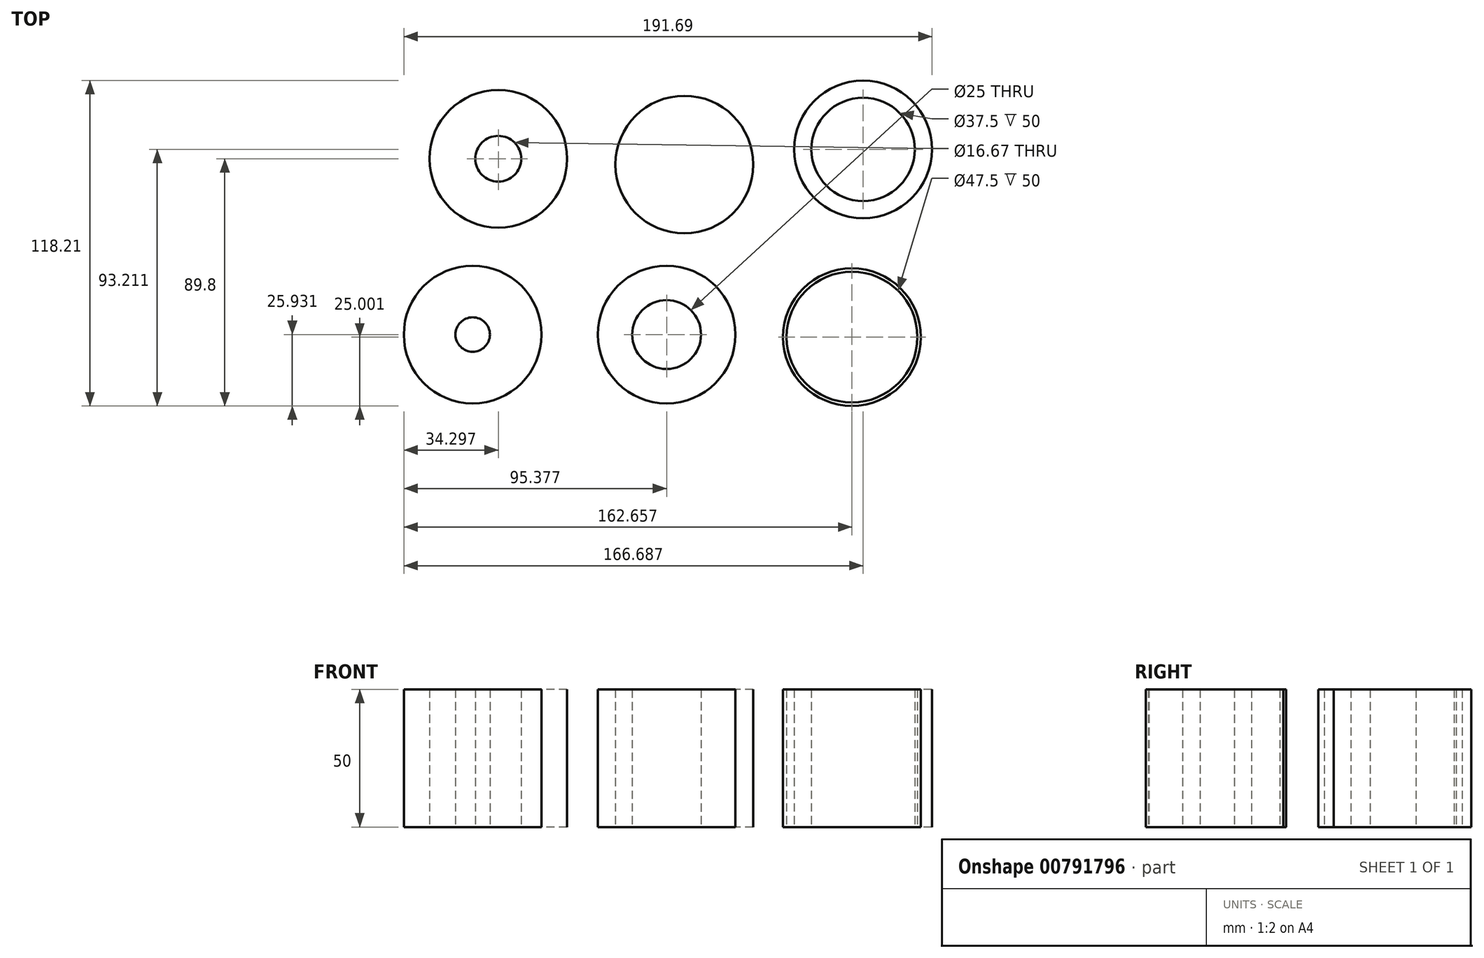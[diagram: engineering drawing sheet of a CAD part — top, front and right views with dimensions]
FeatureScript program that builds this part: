
annotation { "Feature Type Name" : "Feature", "Feature Type Description" : "" }
export const myFeature = defineFeature(function(context is Context, id is Id, definition is map)
    precondition{}
    {
        {
            var Q0;
            Q0=qCreatedBy(makeId("Top.planeOp"),FACE);
            var sketch = newSketch(context, id + "F0", { "sketchPlane" : qUnion([Q0])});
            skCircle(sketch, "E0", {"center": v(-30.83, 32.84) * mm, "radius": 25 * mm});
            skCircle(sketch, "E1", {"center": v(34.04, 38.36) * mm, "radius": 25 * mm});
            skCircle(sketch, "E2", {"center": v(30, -29.85) * mm, "radius": 25 * mm});
            skCircle(sketch, "E3", {"center": v(-37.27, -28.92) * mm, "radius": 25 * mm});
            skCircle(sketch, "E4", {"center": v(-98.35, 34.95) * mm, "radius": 25 * mm});
            skCircle(sketch, "E5", {"center": v(-107.65, -28.92) * mm, "radius": 25 * mm});
            skCircle(sketch, "E6", {"center": v(30, -29.85) * mm, "radius": 23.75 * mm});
            skCircle(sketch, "E7", {"center": v(34.04, 38.36) * mm, "radius": 18.75 * mm});
            skCircle(sketch, "E8", {"center": v(-37.27, -28.92) * mm, "radius": 12.5 * mm});
            skCircle(sketch, "E9", {"center": v(-107.65, -28.92) * mm, "radius": 6.25 * mm});
            skCircle(sketch, "E10", {"center": v(-98.35, 34.95) * mm, "radius": 8.33 * mm});
            skSolve(sketch);
        }
        {
            var Q0;
            Q0=makeQuery(id+"F0.imprint","IMPRINT",FACE,{"disambiguationData":[TD([[makeQuery(id+"F0.imprint","IMPRINT",EDGE,{"derivedFrom":sQuery(id+"F0.wireOp",EDGE,"E4")}),1.0]])]});
            var Q1;
            Q1=makeQuery(id+"F0.imprint","IMPRINT",FACE,{"disambiguationData":[TD([[makeQuery(id+"F0.imprint","IMPRINT",EDGE,{"derivedFrom":sQuery(id+"F0.wireOp",EDGE,"E0")}),1.0]])]});
            var Q2;
            Q2=makeQuery(id+"F0.imprint","IMPRINT",FACE,{"disambiguationData":[TD([[makeQuery(id+"F0.imprint","IMPRINT",EDGE,{"derivedFrom":sQuery(id+"F0.wireOp",EDGE,"E1")}),1.0]])]});
            var Q3;
            Q3=makeQuery(id+"F0.imprint","IMPRINT",FACE,{"disambiguationData":[TD([[makeQuery(id+"F0.imprint","IMPRINT",EDGE,{"derivedFrom":sQuery(id+"F0.wireOp",EDGE,"E5")}),1.0]])]});
            var Q4;
            Q4=makeQuery(id+"F0.imprint","IMPRINT",FACE,{"disambiguationData":[TD([[makeQuery(id+"F0.imprint","IMPRINT",EDGE,{"derivedFrom":sQuery(id+"F0.wireOp",EDGE,"E3")}),1.0]])]});
            var Q5;
            Q5=makeQuery(id+"F0.imprint","IMPRINT",FACE,{"disambiguationData":[TD([[makeQuery(id+"F0.imprint","IMPRINT",EDGE,{"derivedFrom":sQuery(id+"F0.wireOp",EDGE,"E2")}),1.0]])]});
            extrude(context, id + "F1", {"entities" : qUnion([Q0, Q1, Q2, Q3, Q4, Q5]), "depth" : 50 * mm, "offsetDistance" : 25 * mm});
        }
    });
